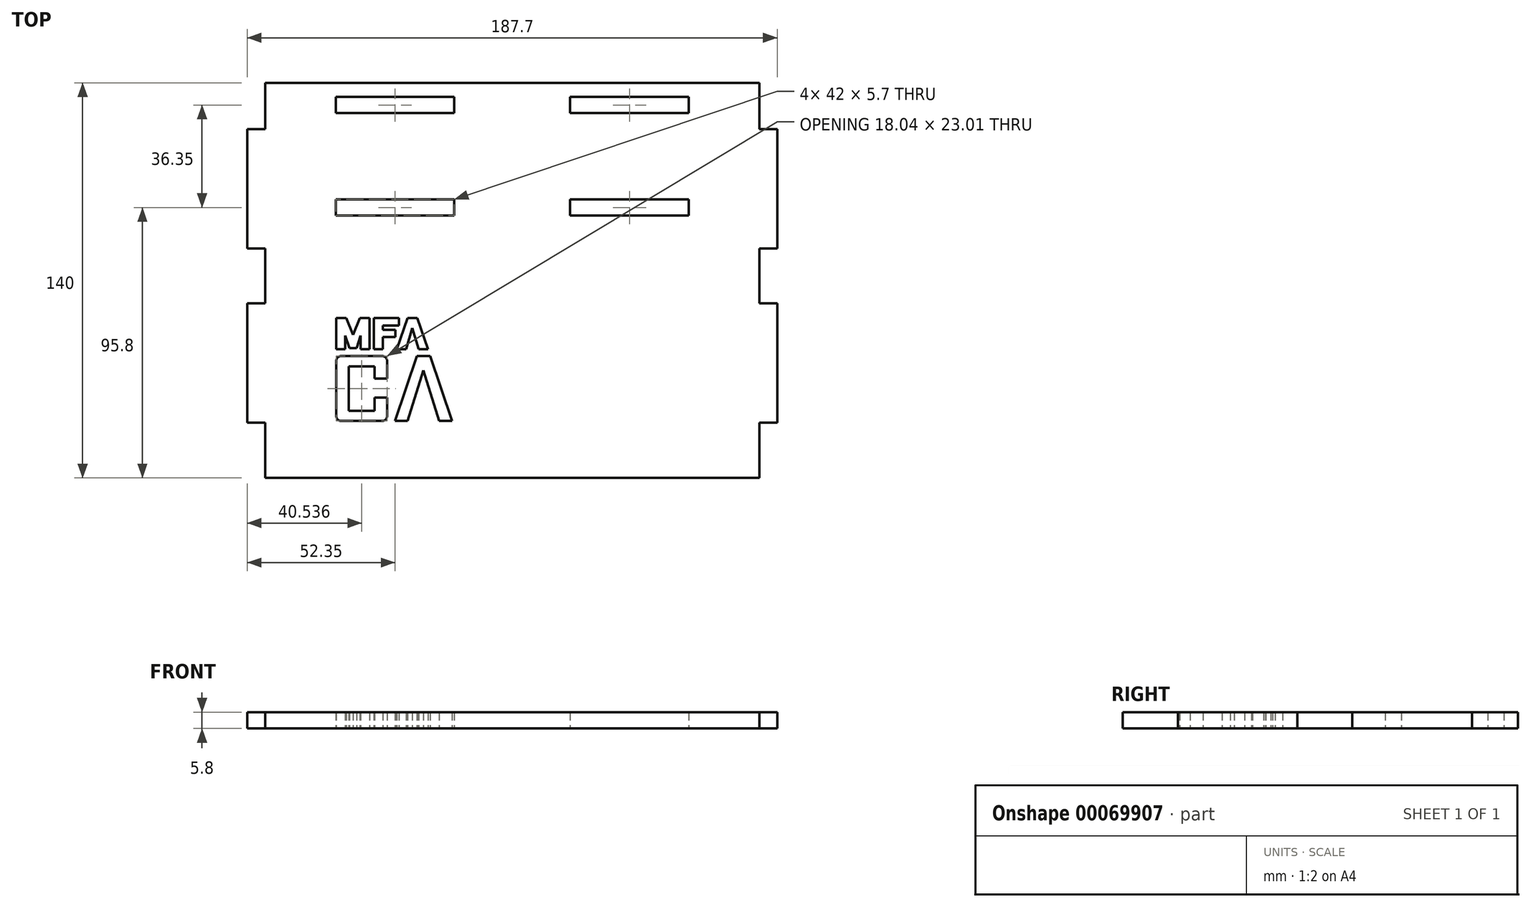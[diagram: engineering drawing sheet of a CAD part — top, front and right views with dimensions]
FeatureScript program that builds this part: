
annotation { "Feature Type Name" : "Feature", "Feature Type Description" : "" }
export const myFeature = defineFeature(function(context is Context, id is Id, definition is map)
    precondition{}
    {
        {
            var Q0;
            Q0=qCreatedBy(makeId("Top.planeOp"),FACE);
            var sketch = newSketch(context, id + "F0", { "sketchPlane" : qUnion([Q0])});
            skLineSegment(sketch, "E0.bottom", {"start": v(87.5, 70) * mm, "end": v(-87.5, 70) * mm});
            skLineSegment(sketch, "E0.top", {"start": v(87.5, -70) * mm, "end": v(-87.5, -70) * mm});
            skLineSegment(sketch, "E0.left", {"start": v(87.5, 70) * mm, "end": v(87.5, 53.65) * mm});
            skLineSegment(sketch, "E0.right", {"start": v(-87.5, 70) * mm, "end": v(-87.5, 53.65) * mm});
            skPoint(sketch, "E0.middle", {"position": v(0, 0) * mm});
            skLineSegment(sketch, "E1.bottom", {"start": v(87.5, 53.65) * mm, "end": v(93.85, 53.65) * mm});
            skLineSegment(sketch, "E1.top", {"start": v(87.5, 11.35) * mm, "end": v(93.85, 11.35) * mm});
            skLineSegment(sketch, "E1.right", {"start": v(93.85, 53.65) * mm, "end": v(93.85, 11.35) * mm});
            skLineSegment(sketch, "E2.trimOffspring", {"start": v(87.5, 11.35) * mm, "end": v(87.5, -8.17) * mm});
            skLineSegment(sketch, "E3.bottom", {"start": v(87.5, -50.48) * mm, "end": v(93.85, -50.48) * mm});
            skLineSegment(sketch, "E3.top", {"start": v(87.5, -8.17) * mm, "end": v(93.85, -8.17) * mm});
            skLineSegment(sketch, "E3.right", {"start": v(93.85, -50.48) * mm, "end": v(93.85, -8.17) * mm});
            skLineSegment(sketch, "E4.trimOffspring", {"start": v(87.5, -50.48) * mm, "end": v(87.5, -70) * mm});
            skPoint(sketch, "E5", {"position": v(0, 70) * mm});
            skPoint(sketch, "E6", {"position": v(0, -70) * mm});
            skLineSegment(sketch, "E7.bottom", {"start": v(-87.5, 53.65) * mm, "end": v(-93.85, 53.65) * mm});
            skLineSegment(sketch, "E7.top", {"start": v(-87.5, 11.35) * mm, "end": v(-93.85, 11.35) * mm});
            skLineSegment(sketch, "E7.right", {"start": v(-93.85, 53.65) * mm, "end": v(-93.85, 11.35) * mm});
            skLineSegment(sketch, "E8.bottom", {"start": v(-87.5, -8.17) * mm, "end": v(-93.85, -8.17) * mm});
            skLineSegment(sketch, "E8.top", {"start": v(-87.5, -50.48) * mm, "end": v(-93.85, -50.48) * mm});
            skLineSegment(sketch, "E8.right", {"start": v(-93.85, -8.17) * mm, "end": v(-93.85, -50.48) * mm});
            skLineSegment(sketch, "E9.trimOffspring", {"start": v(-87.5, 11.35) * mm, "end": v(-87.5, -8.17) * mm});
            skLineSegment(sketch, "E10.trimOffspring", {"start": v(-87.5, -50.48) * mm, "end": v(-87.5, -70) * mm});
            skLineSegment(sketch, "E11.bottom", {"start": v(-62.5, 65) * mm, "end": v(-20.5, 65) * mm});
            skLineSegment(sketch, "E11.top", {"start": v(-62.5, 59.3) * mm, "end": v(-20.5, 59.3) * mm});
            skLineSegment(sketch, "E11.left", {"start": v(-62.5, 65) * mm, "end": v(-62.5, 59.3) * mm});
            skLineSegment(sketch, "E11.right", {"start": v(-20.5, 65) * mm, "end": v(-20.5, 59.3) * mm});
            skLineSegment(sketch, "E12.bottom", {"start": v(20.5, 65) * mm, "end": v(62.5, 65) * mm});
            skLineSegment(sketch, "E12.top", {"start": v(20.5, 59.3) * mm, "end": v(62.5, 59.3) * mm});
            skLineSegment(sketch, "E12.left", {"start": v(20.5, 65) * mm, "end": v(20.5, 59.3) * mm});
            skLineSegment(sketch, "E12.right", {"start": v(62.5, 65) * mm, "end": v(62.5, 59.3) * mm});
            skLineSegment(sketch, "E13.bottom", {"start": v(-62.5, 28.65) * mm, "end": v(-20.5, 28.65) * mm});
            skLineSegment(sketch, "E13.top", {"start": v(-62.5, 22.95) * mm, "end": v(-20.5, 22.95) * mm});
            skLineSegment(sketch, "E13.left", {"start": v(-62.5, 28.65) * mm, "end": v(-62.5, 22.95) * mm});
            skLineSegment(sketch, "E13.right", {"start": v(-20.5, 28.65) * mm, "end": v(-20.5, 22.95) * mm});
            skLineSegment(sketch, "E14.bottom", {"start": v(20.5, 28.65) * mm, "end": v(62.5, 28.65) * mm});
            skLineSegment(sketch, "E14.top", {"start": v(20.5, 22.95) * mm, "end": v(62.5, 22.95) * mm});
            skLineSegment(sketch, "E14.left", {"start": v(20.5, 28.65) * mm, "end": v(20.5, 22.95) * mm});
            skLineSegment(sketch, "E14.right", {"start": v(62.5, 28.65) * mm, "end": v(62.5, 22.95) * mm});
            skLineSegment(sketch, "E15", {"start": v(-46.1, -49.82) * mm, "end": v(-60.53, -49.82) * mm});
            skLineSegment(sketch, "E16", {"start": v(-62.33, -48.02) * mm, "end": v(-62.33, -28.61) * mm});
            skLineSegment(sketch, "E17", {"start": v(-60.53, -26.81) * mm, "end": v(-46.1, -26.81) * mm});
            skLineSegment(sketch, "E18", {"start": v(-44.3, -28.61) * mm, "end": v(-44.3, -34.8) * mm});
            skLineSegment(sketch, "E19", {"start": v(-44.3, -34.8) * mm, "end": v(-48.72, -34.8) * mm});
            skLineSegment(sketch, "E20", {"start": v(-48.72, -34.8) * mm, "end": v(-48.72, -30.46) * mm});
            skLineSegment(sketch, "E21", {"start": v(-48.72, -30.46) * mm, "end": v(-57.9, -30.46) * mm});
            skLineSegment(sketch, "E22", {"start": v(-57.9, -30.46) * mm, "end": v(-57.9, -46.18) * mm});
            skLineSegment(sketch, "E23", {"start": v(-57.9, -46.18) * mm, "end": v(-48.72, -46.18) * mm});
            skLineSegment(sketch, "E24", {"start": v(-48.72, -46.18) * mm, "end": v(-48.72, -41.57) * mm});
            skLineSegment(sketch, "E25", {"start": v(-48.72, -41.57) * mm, "end": v(-44.3, -41.57) * mm});
            skLineSegment(sketch, "E26", {"start": v(-44.3, -41.57) * mm, "end": v(-44.3, -48.02) * mm});
            skLineSegment(sketch, "E27", {"start": v(-41.52, -49.76) * mm, "end": v(-33.76, -26.81) * mm});
            skLineSegment(sketch, "E28", {"start": v(-33.76, -26.81) * mm, "end": v(-29.06, -26.81) * mm});
            skLineSegment(sketch, "E29", {"start": v(-29.06, -26.81) * mm, "end": v(-21.29, -49.76) * mm});
            skLineSegment(sketch, "E30", {"start": v(-21.29, -49.76) * mm, "end": v(-25.83, -49.82) * mm});
            skLineSegment(sketch, "E31", {"start": v(-25.83, -49.82) * mm, "end": v(-31.44, -31.84) * mm});
            skLineSegment(sketch, "E32", {"start": v(-31.44, -31.84) * mm, "end": v(-37, -49.82) * mm});
            skLineSegment(sketch, "E33", {"start": v(-37, -49.82) * mm, "end": v(-41.52, -49.76) * mm});
            skLineSegment(sketch, "E34", {"start": v(-62.3, -24.43) * mm, "end": v(-59.1, -24.43) * mm});
            skLineSegment(sketch, "E35", {"start": v(-59.1, -24.43) * mm, "end": v(-59.1, -19.5) * mm});
            skLineSegment(sketch, "E36", {"start": v(-59.1, -19.5) * mm, "end": v(-57.7, -23.96) * mm});
            skLineSegment(sketch, "E37", {"start": v(-57.7, -23.96) * mm, "end": v(-55.06, -23.96) * mm});
            skLineSegment(sketch, "E38", {"start": v(-55.06, -23.96) * mm, "end": v(-53.66, -19.5) * mm});
            skLineSegment(sketch, "E39", {"start": v(-53.66, -19.5) * mm, "end": v(-53.66, -24.43) * mm});
            skLineSegment(sketch, "E40", {"start": v(-53.66, -24.43) * mm, "end": v(-50.5, -24.43) * mm});
            skLineSegment(sketch, "E41", {"start": v(-50.5, -24.43) * mm, "end": v(-50.5, -13.4) * mm});
            skLineSegment(sketch, "E42", {"start": v(-50.5, -13.4) * mm, "end": v(-53.94, -13.4) * mm});
            skLineSegment(sketch, "E43", {"start": v(-53.94, -13.4) * mm, "end": v(-56.35, -19.32) * mm});
            skLineSegment(sketch, "E44", {"start": v(-56.35, -19.32) * mm, "end": v(-58.84, -13.4) * mm});
            skLineSegment(sketch, "E45", {"start": v(-58.84, -13.4) * mm, "end": v(-62.3, -13.4) * mm});
            skLineSegment(sketch, "E46", {"start": v(-62.3, -13.4) * mm, "end": v(-62.3, -24.43) * mm});
            skLineSegment(sketch, "E47", {"start": v(-45.77, -24.43) * mm, "end": v(-49.04, -24.43) * mm});
            skLineSegment(sketch, "E48", {"start": v(-49.04, -24.43) * mm, "end": v(-49.04, -13.4) * mm});
            skLineSegment(sketch, "E49", {"start": v(-49.04, -13.4) * mm, "end": v(-40.13, -13.4) * mm});
            skLineSegment(sketch, "E50", {"start": v(-40.13, -13.4) * mm, "end": v(-40.13, -16.05) * mm});
            skLineSegment(sketch, "E51", {"start": v(-40.13, -16.05) * mm, "end": v(-45.77, -16.05) * mm});
            skLineSegment(sketch, "E52", {"start": v(-45.77, -16.05) * mm, "end": v(-45.77, -17.56) * mm});
            skLineSegment(sketch, "E53", {"start": v(-45.77, -17.56) * mm, "end": v(-41.4, -17.56) * mm});
            skLineSegment(sketch, "E54", {"start": v(-41.4, -17.56) * mm, "end": v(-41.4, -20.07) * mm});
            skLineSegment(sketch, "E55", {"start": v(-41.4, -20.07) * mm, "end": v(-45.77, -20.07) * mm});
            skLineSegment(sketch, "E56", {"start": v(-45.77, -20.07) * mm, "end": v(-45.77, -24.43) * mm});
            skLineSegment(sketch, "E57", {"start": v(-40.93, -24.4) * mm, "end": v(-37.6, -24.43) * mm});
            skLineSegment(sketch, "E58", {"start": v(-37.6, -24.43) * mm, "end": v(-35.38, -16.92) * mm});
            skLineSegment(sketch, "E59", {"start": v(-35.38, -16.92) * mm, "end": v(-33.17, -24.43) * mm});
            skLineSegment(sketch, "E60", {"start": v(-33.17, -24.43) * mm, "end": v(-29.82, -24.4) * mm});
            skLineSegment(sketch, "E61", {"start": v(-29.82, -24.4) * mm, "end": v(-33.63, -13.4) * mm});
            skLineSegment(sketch, "E62", {"start": v(-33.63, -13.4) * mm, "end": v(-37.11, -13.4) * mm});
            skLineSegment(sketch, "E63", {"start": v(-37.11, -13.4) * mm, "end": v(-40.93, -24.4) * mm});
            skPoint(sketch, "E64.visualSharp", {"position": v(-62.33, -26.81) * mm});
            skArc(sketch, "E64.filletArc", {"start": v(-60.53, -26.81) * mm, "mid": v(-61.8, -27.34) * mm, "end": v(-62.33, -28.61) * mm});
            skPoint(sketch, "E65.visualSharp", {"position": v(-44.3, -26.81) * mm});
            skArc(sketch, "E65.filletArc", {"start": v(-44.3, -28.61) * mm, "mid": v(-44.82, -27.34) * mm, "end": v(-46.1, -26.81) * mm});
            skPoint(sketch, "E66.visualSharp", {"position": v(-44.3, -49.82) * mm});
            skArc(sketch, "E66.filletArc", {"start": v(-46.1, -49.82) * mm, "mid": v(-44.82, -49.3) * mm, "end": v(-44.3, -48.02) * mm});
            skPoint(sketch, "E67.visualSharp", {"position": v(-62.33, -49.82) * mm});
            skArc(sketch, "E67.filletArc", {"start": v(-62.33, -48.02) * mm, "mid": v(-61.8, -49.3) * mm, "end": v(-60.53, -49.82) * mm});
            skSolve(sketch);
        }
        {
            var Q0;
            Q0=makeQuery(id+"F0.imprint","IMPRINT",FACE,{"disambiguationData":[TD([[makeQuery(id+"F0.imprint","IMPRINT",EDGE,{"derivedFrom":sQuery(id+"F0.wireOp",EDGE,"E0.bottom")}),1.0]])]});
            extrude(context, id + "F1", {"entities" : qUnion([Q0]), "depth" : 5.8 * mm});
        }
    });
